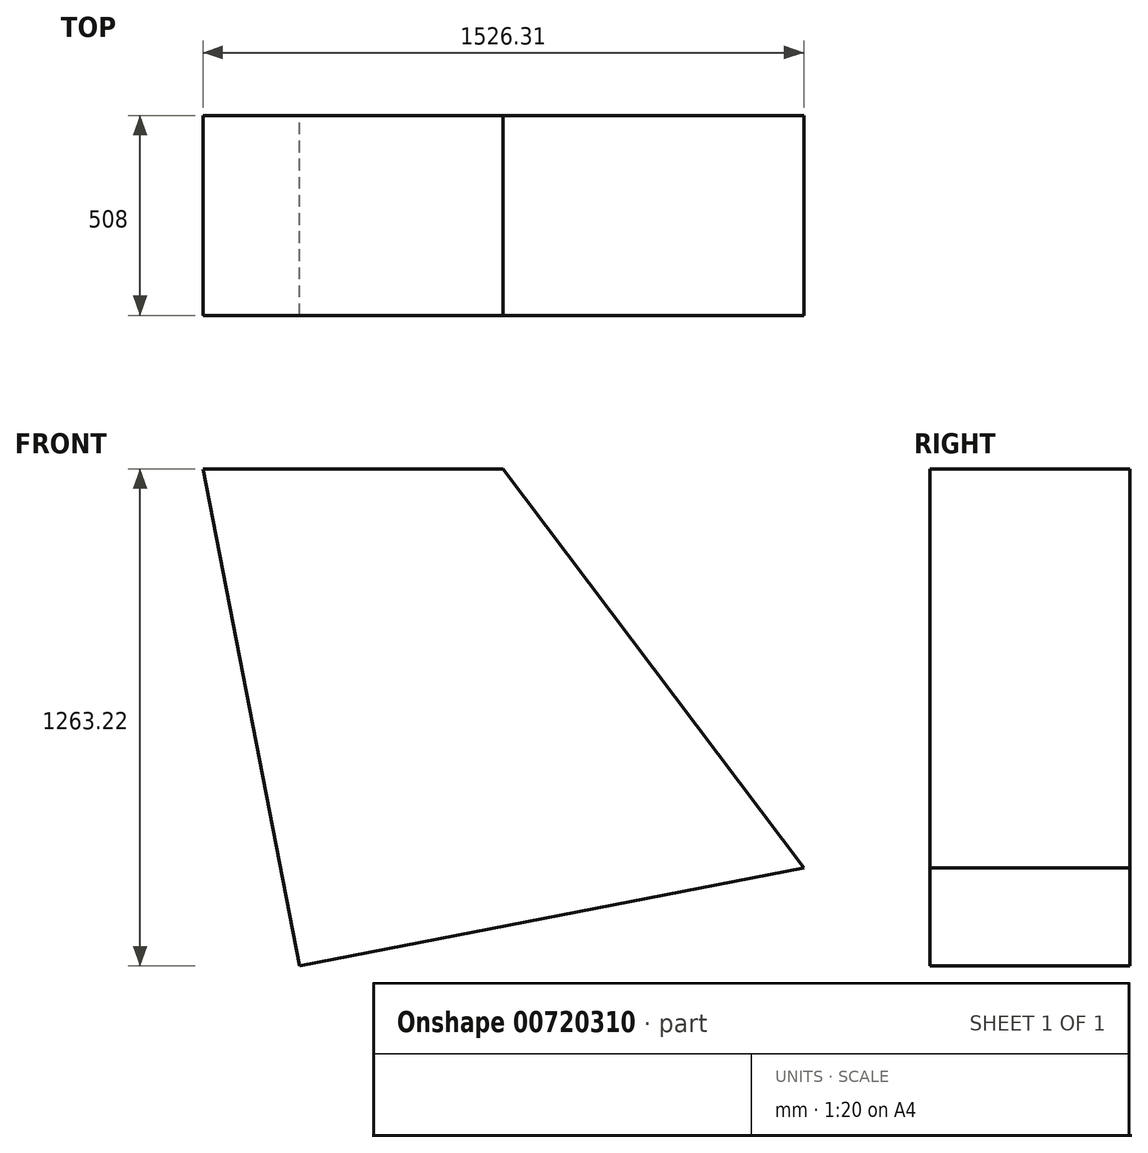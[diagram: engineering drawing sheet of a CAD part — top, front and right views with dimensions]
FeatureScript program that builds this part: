
annotation { "Feature Type Name" : "Feature", "Feature Type Description" : "" }
export const myFeature = defineFeature(function(context is Context, id is Id, definition is map)
    precondition{}
    {
        {
            var Q0;
            Q0=qCreatedBy(makeId("Front.planeOp"),FACE);
            var sketch = newSketch(context, id + "F0", { "sketchPlane" : qUnion([Q0])});
            skLineSegment(sketch, "E0", {"start": v(0, 0) * mm, "end": v(1280.76, 248.95) * mm});
            skLineSegment(sketch, "E1", {"start": v(1280.76, 248.95) * mm, "end": v(516.45, 1263.22) * mm});
            skLineSegment(sketch, "E2", {"start": v(516.45, 1263.22) * mm, "end": v(-245.55, 1263.22) * mm});
            skLineSegment(sketch, "E3", {"start": v(-245.55, 1263.22) * mm, "end": v(0, 0) * mm});
            skSolve(sketch);
        }
        {
            var Q0;
            Q0=makeQuery(id+"F0.imprint","IMPRINT",FACE,{"disambiguationData":[TD([[makeQuery(id+"F0.imprint","IMPRINT",EDGE,{"derivedFrom":sQuery(id+"F0.wireOp",EDGE,"E0")}),1.0]])]});
            extrude(context, id + "F1", {"entities" : qUnion([Q0]), "depth" : 508 * mm, "offsetDistance" : 25.4 * mm});
        }
    });
